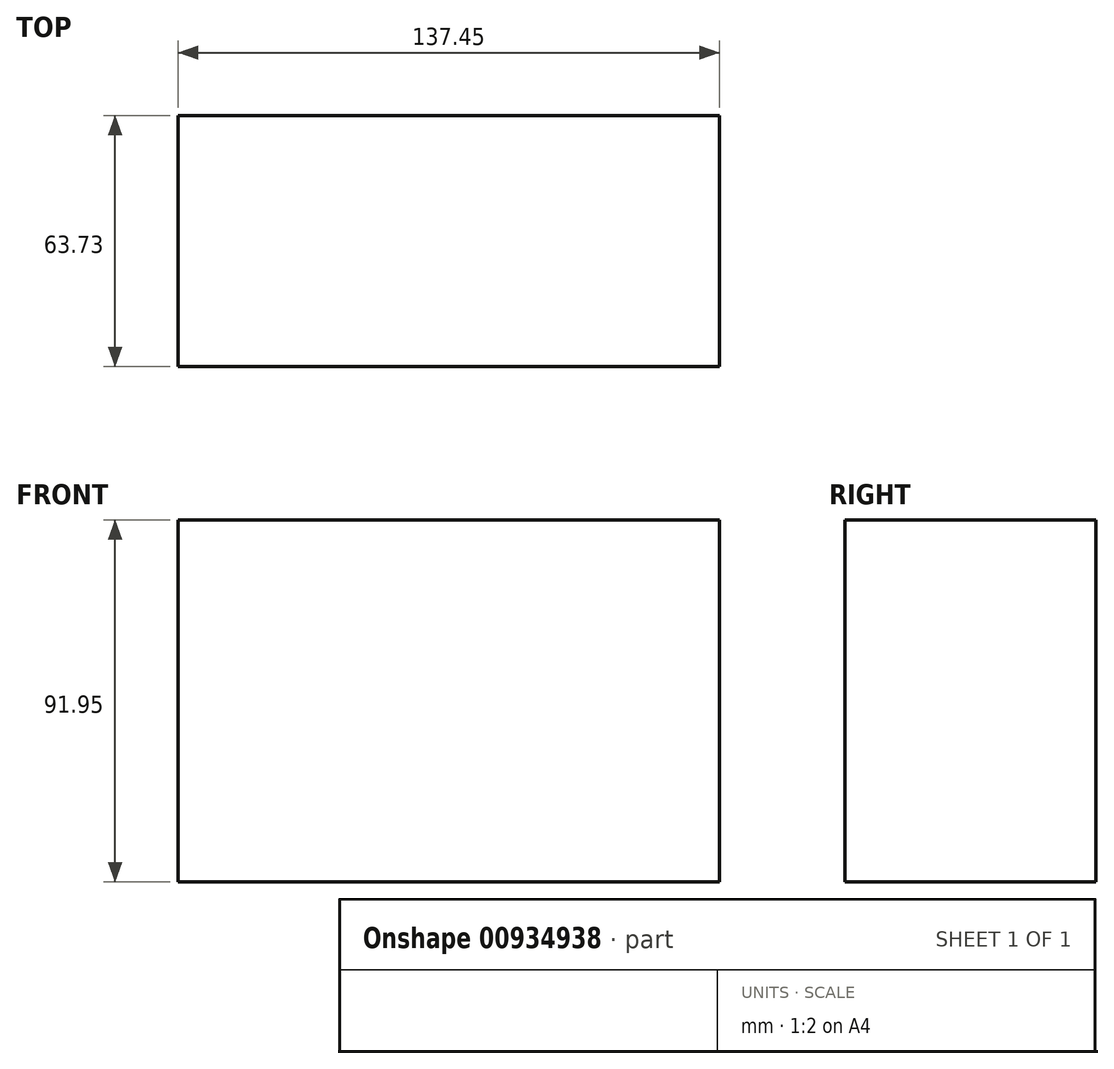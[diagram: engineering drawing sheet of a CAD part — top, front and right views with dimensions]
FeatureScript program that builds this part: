
annotation { "Feature Type Name" : "Feature", "Feature Type Description" : "" }
export const myFeature = defineFeature(function(context is Context, id is Id, definition is map)
    precondition{}
    {
        {
            var Q0;
            Q0=qCreatedBy(makeId("Top.planeOp"),FACE);
            var sketch = newSketch(context, id + "F0", { "sketchPlane" : qUnion([Q0])});
            skLineSegment(sketch, "E0.bottom", {"start": v(-77.98, 31.28) * mm, "end": v(59.47, 31.28) * mm});
            skLineSegment(sketch, "E0.top", {"start": v(-77.98, -32.45) * mm, "end": v(59.47, -32.45) * mm});
            skLineSegment(sketch, "E0.left", {"start": v(-77.98, 31.28) * mm, "end": v(-77.98, -32.45) * mm});
            skLineSegment(sketch, "E0.right", {"start": v(59.47, 31.28) * mm, "end": v(59.47, -32.45) * mm});
            skSolve(sketch);
        }
        {
            var Q0;
            Q0 = qSketchRegion(id + "F0", true);
            extrude(context, id + "F1", {"entities" : qUnion([Q0]), "depth" : 91.95 * mm, "offsetDistance" : 25.4 * mm});
        }
    });
